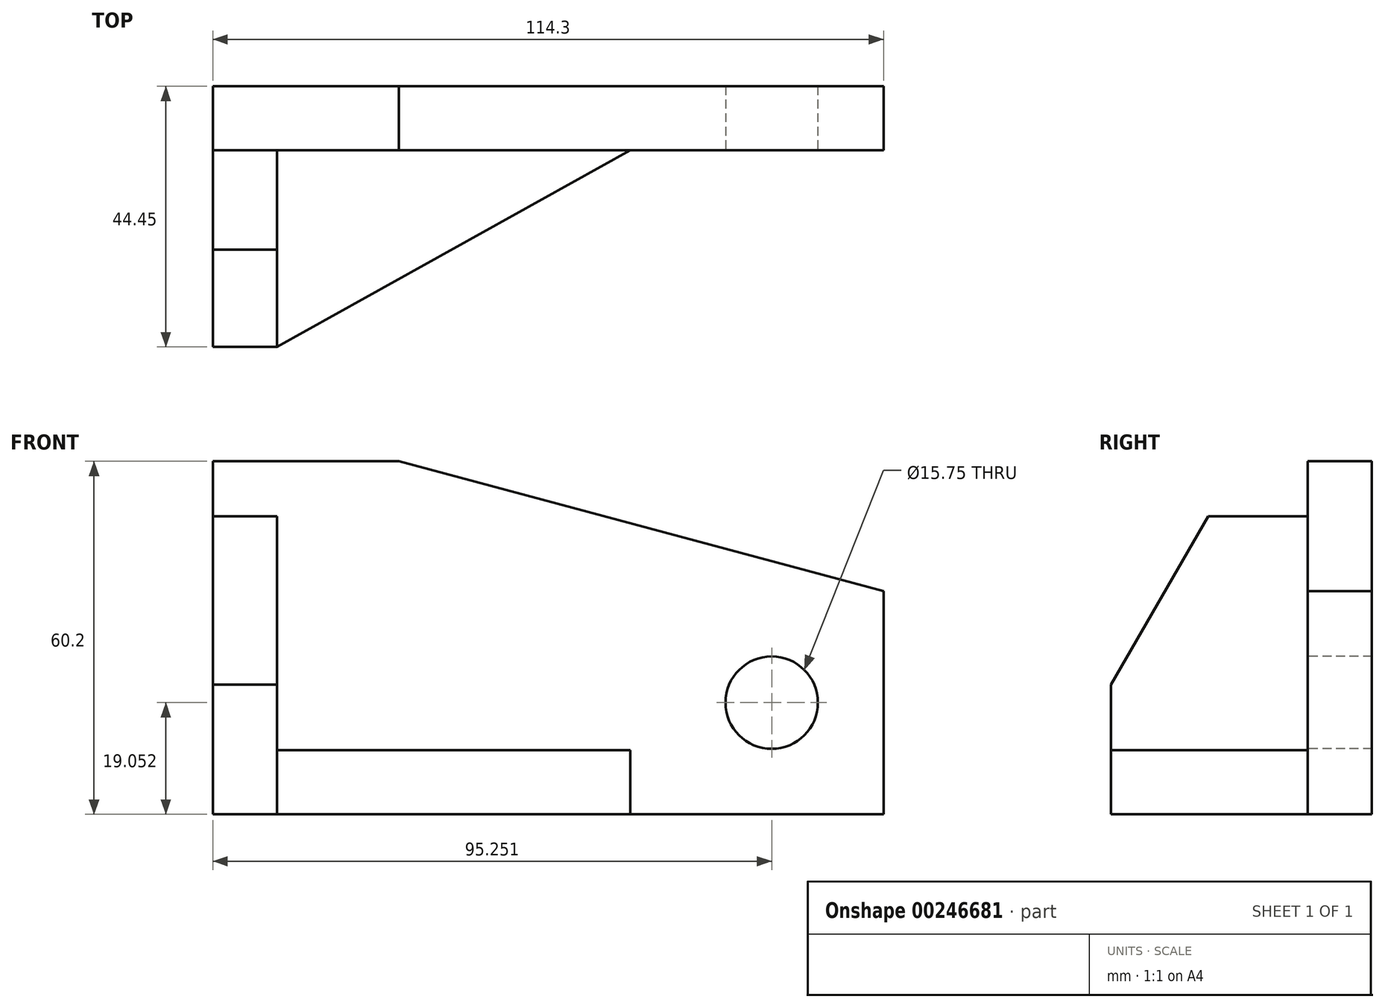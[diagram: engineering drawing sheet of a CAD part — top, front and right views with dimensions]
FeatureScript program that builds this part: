
annotation { "Feature Type Name" : "Feature", "Feature Type Description" : "" }
export const myFeature = defineFeature(function(context is Context, id is Id, definition is map)
    precondition{}
    {
        {
            var Q0;
            Q0=qCreatedBy(makeId("Front.planeOp"),FACE);
            var sketch = newSketch(context, id + "F0", { "sketchPlane" : qUnion([Q0])});
            skLineSegment(sketch, "E0", {"start": v(-92.86, 15.51) * mm, "end": v(-92.86, -44.69) * mm});
            skLineSegment(sketch, "E1", {"start": v(-92.86, 15.51) * mm, "end": v(-61.1, 15.51) * mm});
            skLineSegment(sketch, "E2", {"start": v(-61.1, 15.51) * mm, "end": v(21.44, -6.6) * mm});
            skLineSegment(sketch, "E3", {"start": v(-92.86, -44.69) * mm, "end": v(21.44, -44.69) * mm});
            skLineSegment(sketch, "E4", {"start": v(21.44, -6.6) * mm, "end": v(21.44, -44.69) * mm});
            skSolve(sketch);
        }
        {
            var Q0;
            Q0 = qSketchRegion(id + "F0", true);
            extrude(context, id + "F1", {"entities" : qUnion([Q0]), "depth" : 10.92 * mm});
        }
        {
            var Q0;
            Q0=makeQuery(id+"F1.opExtrude","CAP_FACE",FACE,{"disambiguationData":[OSD([sQuery(id+"F0.wireOp",EDGE,"E0"),sQuery(id+"F0.wireOp",EDGE,"E1"),sQuery(id+"F0.wireOp",EDGE,"E2"),sQuery(id+"F0.wireOp",EDGE,"E3"),sQuery(id+"F0.wireOp",EDGE,"E4")])],"isStart":false});
            var sketch = newSketch(context, id + "F2", { "sketchPlane" : qUnion([Q0])});
            skLineSegment(sketch, "E5.bottom", {"start": v(-92.86, 6.11) * mm, "end": v(-81.94, 6.11) * mm});
            skLineSegment(sketch, "E5.top", {"start": v(-92.86, -44.69) * mm, "end": v(-81.94, -44.69) * mm});
            skLineSegment(sketch, "E5.left", {"start": v(-92.86, 6.11) * mm, "end": v(-92.86, -44.69) * mm});
            skLineSegment(sketch, "E5.right", {"start": v(-81.94, 6.11) * mm, "end": v(-81.94, -44.69) * mm});
            skSolve(sketch);
        }
        {
            var Q0;
            Q0 = qSketchRegion(id + "F2", true);
            extrude(context, id + "F3", {"entities" : qUnion([Q0]), "operationType" : NewBodyOperationType.ADD, "depth" : 33.53 * mm});
        }
        {
            var Q0;
            Q0=makeQuery(id+"F1.opExtrude","CAP_FACE",FACE,{"disambiguationData":[OSD([sQuery(id+"F0.wireOp",EDGE,"E0"),sQuery(id+"F0.wireOp",EDGE,"E1"),sQuery(id+"F0.wireOp",EDGE,"E2"),sQuery(id+"F0.wireOp",EDGE,"E3"),sQuery(id+"F0.wireOp",EDGE,"E4")])],"isStart":false});
            var sketch = newSketch(context, id + "F4", { "sketchPlane" : qUnion([Q0])});
            skLineSegment(sketch, "E6.bottom", {"start": v(-81.94, -44.69) * mm, "end": v(-21.74, -44.69) * mm});
            skLineSegment(sketch, "E6.top", {"start": v(-81.94, -33.77) * mm, "end": v(-21.74, -33.77) * mm});
            skLineSegment(sketch, "E6.left", {"start": v(-81.94, -44.69) * mm, "end": v(-81.94, -33.77) * mm});
            skLineSegment(sketch, "E6.right", {"start": v(-21.74, -44.69) * mm, "end": v(-21.74, -33.77) * mm});
            skSolve(sketch);
        }
        {
            var Q0;
            Q0=makeQuery(id+"F4.imprint","IMPRINT",FACE,{"disambiguationData":[TD([[makeQuery(id+"F4.imprint","IMPRINT",EDGE,{"derivedFrom":sQuery(id+"F4.wireOp",EDGE,"E6.bottom")}),1.0]])]});
            extrude(context, id + "F5", {"entities" : qUnion([Q0]), "operationType" : NewBodyOperationType.ADD, "depth" : 33.53 * mm});
        }
        {
            var Q0;
            Q0=makeQuery(id+"F5.opExtrude","SWEPT_FACE",FACE,{"disambiguationData":[OSD([sQuery(id+"F4.wireOp",EDGE,"E6.top")])]});
            var sketch = newSketch(context, id + "F6", { "sketchPlane" : qUnion([Q0])});
            skLineSegment(sketch, "E7", {"start": v(-81.94, -44.45) * mm, "end": v(-21.74, -10.92) * mm});
            skSolve(sketch);
        }
        {
            var Q0;
            Q0 = qSketchRegion(id + "F6", true);
            var Q1;
            Q1=makeQuery(id+"F6.imprint","IMPRINT",FACE,{"disambiguationData":[TD([[makeQuery(id+"F6.imprint","IMPRINT",EDGE,{"derivedFrom":sQuery(id+"F6.wireOp",EDGE,"E7")}),-1.0]])]});
            extrude(context, id + "F7", {"entities" : qUnion([Q0, Q1]), "operationType" : NewBodyOperationType.REMOVE, "oppositeDirection" : true, "depth" : 25.4 * mm});
        }
        {
            var Q0;
            Q0=makeQuery(id+"F1.opExtrude","CAP_FACE",FACE,{"disambiguationData":[OSD([sQuery(id+"F0.wireOp",EDGE,"E0"),sQuery(id+"F0.wireOp",EDGE,"E1"),sQuery(id+"F0.wireOp",EDGE,"E2"),sQuery(id+"F0.wireOp",EDGE,"E3"),sQuery(id+"F0.wireOp",EDGE,"E4")])],"isStart":false});
            var sketch = newSketch(context, id + "F8", { "sketchPlane" : qUnion([Q0])});
            skLineSegment(sketch, "E8", {"start": v(2.4, -44.69) * mm, "end": v(2.4, -25.64) * mm});
            skLineSegment(sketch, "E9", {"start": v(2.4, -25.64) * mm, "end": v(21.44, -25.64) * mm});
            skCircle(sketch, "E10", {"center": v(2.4, -25.64) * mm, "radius": 7.87 * mm});
            skSolve(sketch);
        }
        {
            var Q0;
            Q0 = qSketchRegion(id + "F8", true);
            extrude(context, id + "F9", {"entities" : qUnion([Q0]), "operationType" : NewBodyOperationType.REMOVE, "endBound" : BoundingType.THROUGH_ALL, "oppositeDirection" : true, "depth" : 25.4 * mm});
        }
        {
            var Q0;
            Q0=makeQuery(id+"F3.opExtrude","SWEPT_FACE",FACE,{"disambiguationData":[OSD([sQuery(id+"F2.wireOp",EDGE,"E5.right")])]});
            var sketch = newSketch(context, id + "F10", { "sketchPlane" : qUnion([Q0])});
            skPoint(sketch, "E11", {"position": v(-44.45, -22.59) * mm});
            skLineSegment(sketch, "E12", {"start": v(-44.45, -22.59) * mm, "end": v(-27.88, 6.11) * mm});
            skPoint(sketch, "E13", {"position": v(-44.45, -44.69) * mm});
            skSolve(sketch);
        }
        {
            var Q0;
            {var subQ0=sQuery(id+"F10.wireOp",EDGE,"E12");Q0=makeQuery(id+"F10.imprint","IMPRINT",FACE,{"disambiguationData":[TD([[makeQuery(id+"F10.imprint","IMPRINT",EDGE,{"derivedFrom":subQ0}),1.0]])]});}
            extrude(context, id + "F11", {"entities" : qUnion([Q0]), "operationType" : NewBodyOperationType.REMOVE, "endBound" : BoundingType.THROUGH_ALL, "oppositeDirection" : true, "depth" : 25.4 * mm});
        }
    });
